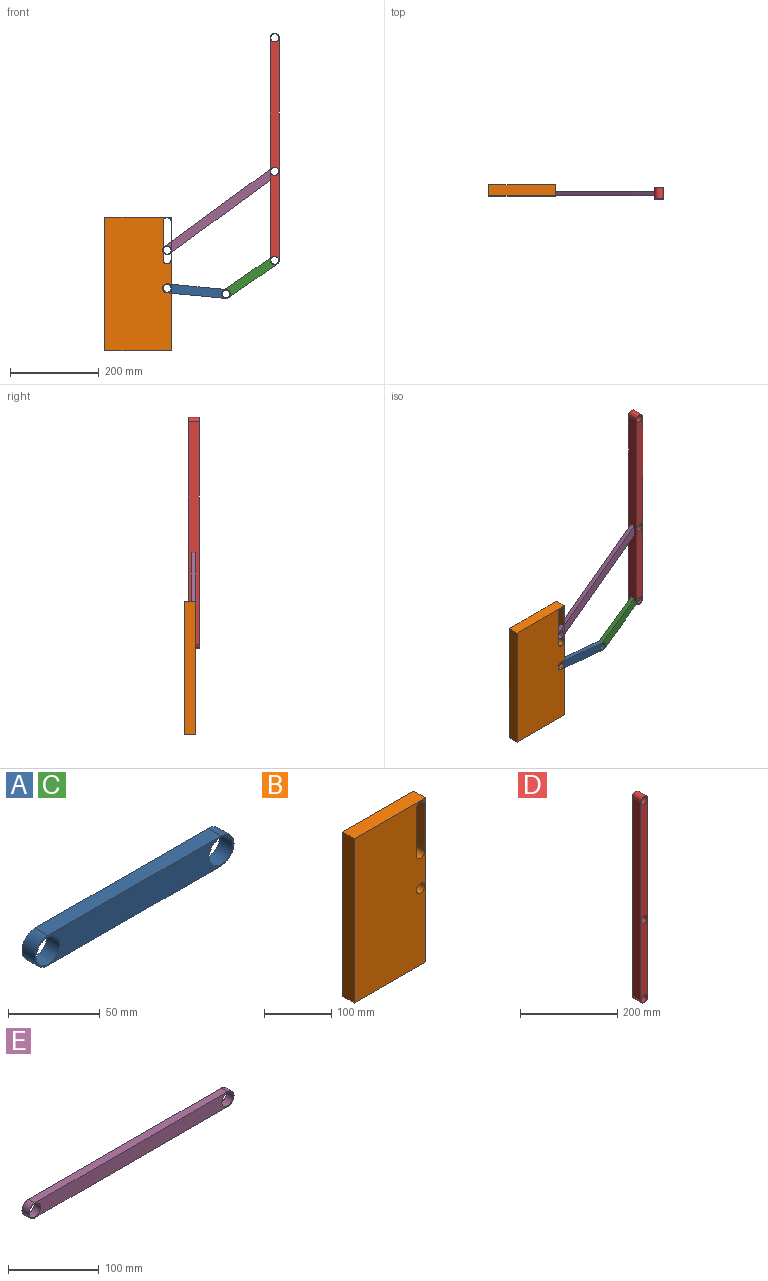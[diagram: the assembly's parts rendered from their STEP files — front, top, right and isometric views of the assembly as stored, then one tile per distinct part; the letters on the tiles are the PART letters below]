
ASSEMBLY  parts=5 mates=6
PART A: 8 faces, bbox 153.1x10x20 mm
  f0: plane 133.08x10mm, normal (0,0,-1), area 1330.8mm2, adj f1,f5,f6,f7
  f1: cylinder r=10mm len=20mm, axis (0,1,0), area 314.2mm2, adj f0,f2,f6,f7
  f2: plane 133.08x10mm, normal (0,0,1), area 1330.8mm2, adj f1,f5,f6,f7
  f3: cylinder r=9mm len=18mm, axis (0,1,0), area 565.5mm2, adj f6,f7
  f4: cylinder r=9mm len=18mm, axis (0,1,0), area 565.5mm2, adj f6,f7
  f5: cylinder r=10mm len=20mm, axis (0,1,0), area 314.2mm2, adj f0,f2,f6,f7
  f6: plane 153.08x20mm, normal (0,-1,0), area 2466.8mm2, adj f0,f1,f2,f3,f4,f5
  f7: plane 153.08x20mm, normal (0,1,0), area 2466.8mm2, adj f0,f1,f2,f3,f4,f5
PART B: 11 faces, bbox 150x25x300 mm
  f0: plane 150x25mm, normal (0,0,1), area 3750mm2, adj f1,f8,f9,f10
  f1: plane 300x25mm, normal (-1,0,0), area 7500mm2, adj f0,f2,f9,f10
  f2: plane 150x25mm, normal (0,0,-1), area 3750mm2, adj f1,f8,f9,f10
  f3: cylinder r=9mm len=25mm, axis (0,1,0), area 706.9mm2, adj f4,f6,f9,f10
  f4: plane 86.27x25mm, normal (1,0,0), area 2156.8mm2, adj f3,f5,f9,f10
  f5: cylinder r=9mm len=25mm, axis (0,1,0), area 706.9mm2, adj f4,f6,f9,f10
  f6: plane 86.27x25mm, normal (-1,0,0), area 2156.8mm2, adj f3,f5,f9,f10
  f7: cylinder r=9mm len=25mm, axis (0,1,0), area 1413.7mm2, adj f9,f10
  f8: plane 300x25mm, normal (1,0,0), area 7500mm2, adj f0,f2,f9,f10
  f9: plane 300x150mm, normal (0,-1,0), area 42938.2mm2, adj f0,f1,f2,f3,f4,f5,f6,f7
  f10: plane 300x150mm, normal (0,1,0), area 42938.2mm2, adj f0,f1,f2,f3,f4,f5,f6,f7
PART C: same geometry as A
PART D: 9 faces, bbox 20x25x520 mm
  f0: cylinder r=10mm len=25mm, axis (0,1,0), area 785.4mm2, adj f1,f3,f7,f8
  f1: plane 500x25mm, normal (-1,0,0), area 12500mm2, adj f0,f2,f7,f8
  f2: cylinder r=10mm len=25mm, axis (0,1,0), area 785.4mm2, adj f1,f3,f7,f8
  f3: plane 500x25mm, normal (1,0,0), area 12500mm2, adj f0,f2,f7,f8
  f4: cylinder r=9mm len=25mm, axis (0,1,0), area 1413.7mm2, adj f7,f8
  f5: cylinder r=9mm len=25mm, axis (0,1,0), area 1413.7mm2, adj f7,f8
  f6: cylinder r=9mm len=25mm, axis (0,1,0), area 1413.7mm2, adj f7,f8
  f7: plane 520x20mm, normal (0,-1,0), area 9550.8mm2, adj f0,f1,f2,f3,f4,f5,f6
  f8: plane 520x20mm, normal (0,1,0), area 9550.8mm2, adj f0,f1,f2,f3,f4,f5,f6
PART E: 8 faces, bbox 320x10x20 mm
  f0: plane 299.97x10mm, normal (0,0,-1), area 2999.7mm2, adj f1,f5,f6,f7
  f1: cylinder r=10mm len=20mm, axis (0,1,0), area 314.2mm2, adj f0,f2,f6,f7
  f2: plane 300x10mm, normal (0,0,1), area 3000mm2, adj f1,f5,f6,f7
  f3: cylinder r=9mm len=18mm, axis (0,1,0), area 565.5mm2, adj f6,f7
  f4: cylinder r=9mm len=18mm, axis (0,1,0), area 565.5mm2, adj f6,f7
  f5: cylinder r=10mm len=20mm, axis (0,1,0), area 314.5mm2, adj f0,f2,f6,f7
  f6: plane 320x20mm, normal (0,-1,0), area 5805.2mm2, adj f0,f1,f2,f3,f4,f5
  f7: plane 320x20mm, normal (0,1,0), area 5805.2mm2, adj f0,f1,f2,f3,f4,f5
PLACE A rot(axis=(0,1,0),5.5deg) t=(6.5,-52.53,9.83)mm
PLACE B t=(17.85,-37.53,29.86)mm fixed
PLACE C rot(axis=(0,-1,0),34.7deg) t=(174.65,-52.53,155.6)mm
PLACE D t=(49.49,-45.03,200.82)mm
PLACE E rot(axis=(-0.95,0,-0.31),180deg) t=(-218.39,-62.53,337.36)mm
MATE planar E.f3 <-> B.f3  axis (0,-1,0) through (-192.43,-62.53,223.41)mm
MATE revolute D.f2 <-> C.f1  axis (0,1,0) through (49.49,-57.53,200.82)mm
MATE revolute A.f1 <-> C.f3  axis (0,-1,0) through (-59.96,-62.53,125.13)mm
MATE revolute E.f1 <-> D.f5  axis (0,-1,0) through (49.49,-57.53,400.82)mm
MATE revolute A.f3 <-> B.f7  axis (0,-1,0) through (-192.43,-62.53,137.9)mm
MATE parallel B.f8 <-> D.f3  axis (1,0,0) through (-182.43,-50.03,147.9)mm
